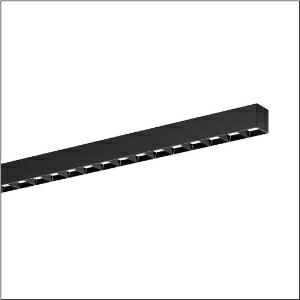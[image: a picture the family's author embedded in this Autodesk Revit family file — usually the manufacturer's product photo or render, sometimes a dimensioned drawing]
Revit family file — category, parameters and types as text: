
# Revit family: silica_r__21_51mx24tat4b_951d
name_source: partatom
category: Lighting Fixtures
units: mm (PartAtom-declared; Revit-internal decimal feet)

## family parameters
Cut with Voids When Loaded = No
Host = Face
Light Source = No
Part Type = Normal
Room Calculation Point = No
Round Connector Dimension = Use Diameter
Shared = No

## types (1)
- --- (1 x LED, 3280 lm, 32.4 W, 6500K)
    Apparent Load = 32 VA
    CIE Flux Codes = 74 94 99 100 100
    Color Rendering = 80
    Color Temperature = 6500K
    Default Elevation = 1800 mm
    Description = Silica® 21, office luminaire, primary light control with darklight reflector, of PMMA, black, light emission: direct distribution, primary light characteristic: asymmetric, installation type: surface-mounted, LED, rated luminous flux: 3.280lm, luminous efficacy: 96lm/W, light colour: 8tw, colour temperature: 2700..6500K, control gear: ECG DALI, with terminal, 3+2-pole, max. 2.5mm², mains connection: 220..240V, AC, 50/60Hz, rated input power: 34.1W, luminaire housing, of aluminium, jet black (RAL 9005), length: 1.204mm, width: 53mm, height: 53mm, protection rating (complete): IP20, insulation class (complete): insulation class I (protective earthing), certification: CE, permissible operating ambient temperature: 0..+35°C, standard: EN 50419, packaging unit: 1 piece
    Height = 0 mm  [stored 0 ft]
    Lamp = 1 x LED
    Lamp Light Flux = 3280 lm
    Lamp Power = 32.4 W
    Lamp count = 1
    Length = 1204 mm
    Luminous efficacy = 101 lm/W
    Manufacturer = Siteco
    ModVariant = No
    Model = 51MX24TAT4B
    Mounting Place = Ceiling
    Mounting Type = Recessed
    Number of Poles = 1
    OnlyDefault = Yes
    Power Factor = 1
    Product Name = Silica® 21
    Product group = office luminaire | ceiling recessed
    ProductGroupID = 401
    Protection Class = Protection class I
    Protection Degree = IP 20
    RLX_Detail_Level = 1
    RLX_Emergency_Light_Flux = 0 lm
    RLX_Emergency_Type = 0
    RLX_Emergency_Type_DB = No
    RlxData = <blob elided: 40793 chars, md5=be8ed557>
    Socket = socket
    Standby Power = 0 W
    System Light Flux = 3280 lm
    System Power = 32 W
    Type Comments = individual setting
    Type Image = l_1297756.jpg
    URL = http://relux.com
    VarID = @adj_071323
    Voltage = 0 V
    Weight = 0.00 kg
    Width = 53 mm

note: [stored X ft] marks values corroborated as IEEE doubles in the binary element streams (Revit-internal decimal feet)

## geometry (parser evidence)
native form markers: Blend x4, Sweep x9
no freeform markers — native parametric forms only
